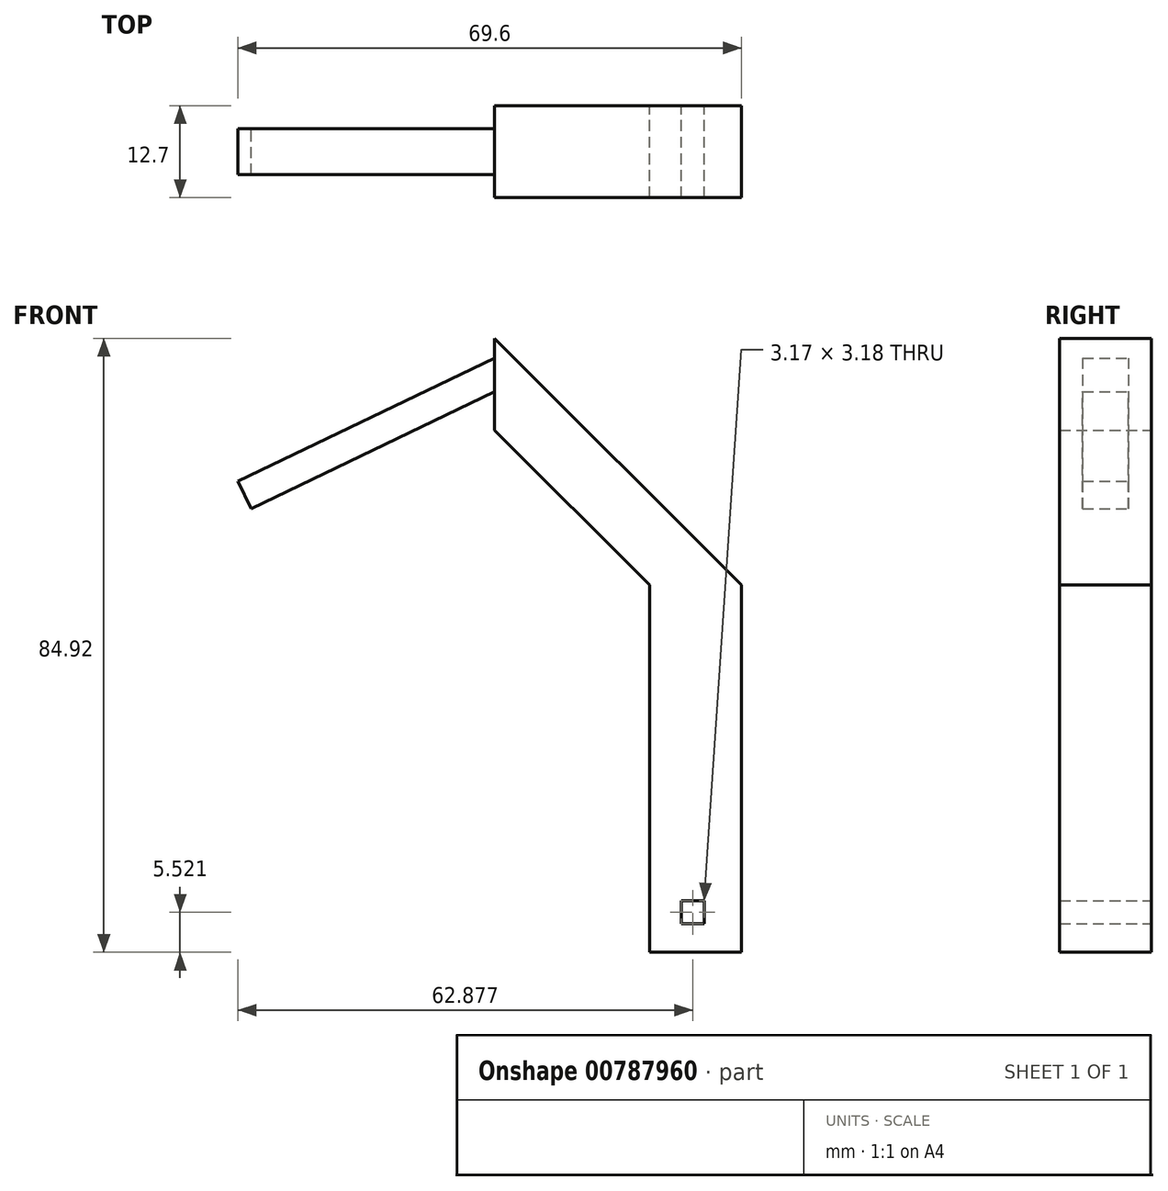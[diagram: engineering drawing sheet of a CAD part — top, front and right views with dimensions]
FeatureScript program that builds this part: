
annotation { "Feature Type Name" : "Feature", "Feature Type Description" : "" }
export const myFeature = defineFeature(function(context is Context, id is Id, definition is map)
    precondition{}
    {
        {
            var Q0;
            Q0=qCreatedBy(makeId("Front.planeOp"),FACE);
            var sketch = newSketch(context, id + "F0", { "sketchPlane" : qUnion([Q0])});
            skLineSegment(sketch, "E0", {"start": v(12.7, -36.87) * mm, "end": v(12.7, 13.93) * mm});
            skLineSegment(sketch, "E1", {"start": v(0, 13.93) * mm, "end": v(12.7, 13.93) * mm});
            skLineSegment(sketch, "E2", {"start": v(12.7, -36.87) * mm, "end": v(0, -36.87) * mm});
            skLineSegment(sketch, "E3", {"start": v(0, -36.87) * mm, "end": v(0, 13.93) * mm});
            skLineSegment(sketch, "E4", {"start": v(12.7, 13.93) * mm, "end": v(-21.42, 48.05) * mm});
            skLineSegment(sketch, "E5", {"start": v(-21.42, 48.05) * mm, "end": v(-21.42, 35.35) * mm});
            skLineSegment(sketch, "E6", {"start": v(-21.42, 35.35) * mm, "end": v(0, 13.93) * mm});
            skLineSegment(sketch, "E7", {"start": v(-21.42, 45.34) * mm, "end": v(-56.9, 28.3) * mm});
            skLineSegment(sketch, "E8", {"start": v(-56.9, 28.3) * mm, "end": v(-55.08, 24.51) * mm});
            skLineSegment(sketch, "E9", {"start": v(-55.08, 24.51) * mm, "end": v(-21.42, 40.69) * mm});
            skPoint(sketch, "E9.endSnap0", {"position": v(-21.42, 41.7) * mm});
            skLineSegment(sketch, "E10.bottom", {"start": v(4.39, -29.76) * mm, "end": v(7.56, -29.76) * mm});
            skLineSegment(sketch, "E10.top", {"start": v(4.39, -32.94) * mm, "end": v(7.56, -32.94) * mm});
            skLineSegment(sketch, "E10.left", {"start": v(4.39, -29.76) * mm, "end": v(4.39, -32.94) * mm});
            skLineSegment(sketch, "E10.right", {"start": v(7.56, -29.76) * mm, "end": v(7.56, -32.94) * mm});
            skSolve(sketch);
        }
        {
            var Q0;
            Q0=makeQuery(id+"F0.imprint","IMPRINT",FACE,{"disambiguationData":[TD([[makeQuery(id+"F0.imprint","IMPRINT",EDGE,{"derivedFrom":sQuery(id+"F0.wireOp",EDGE,"E1")}),1.0]])]});
            var Q1;
            Q1=makeQuery(id+"F0.imprint","IMPRINT",FACE,{"disambiguationData":[TD([[makeQuery(id+"F0.imprint","IMPRINT",EDGE,{"derivedFrom":sQuery(id+"F0.wireOp",EDGE,"E0")}),1.0]])]});
            extrude(context, id + "F1", {"entities" : qUnion([Q0, Q1]), "endBound" : BoundingType.SYMMETRIC, "depth" : 12.7 * mm, "offsetDistance" : 25.4 * mm});
        }
        {
            var Q0;
            {var subQ0=sQuery(id+"F0.wireOp",EDGE,"E7");Q0=makeQuery(id+"F0.imprint","IMPRINT",FACE,{"disambiguationData":[TD([[makeQuery(id+"F0.imprint","IMPRINT",EDGE,{"derivedFrom":subQ0}),1.0]])]});}
            extrude(context, id + "F2", {"entities" : qUnion([Q0]), "operationType" : NewBodyOperationType.ADD, "endBound" : BoundingType.SYMMETRIC, "depth" : 6.35 * mm, "offsetDistance" : 25.4 * mm});
        }
    });
